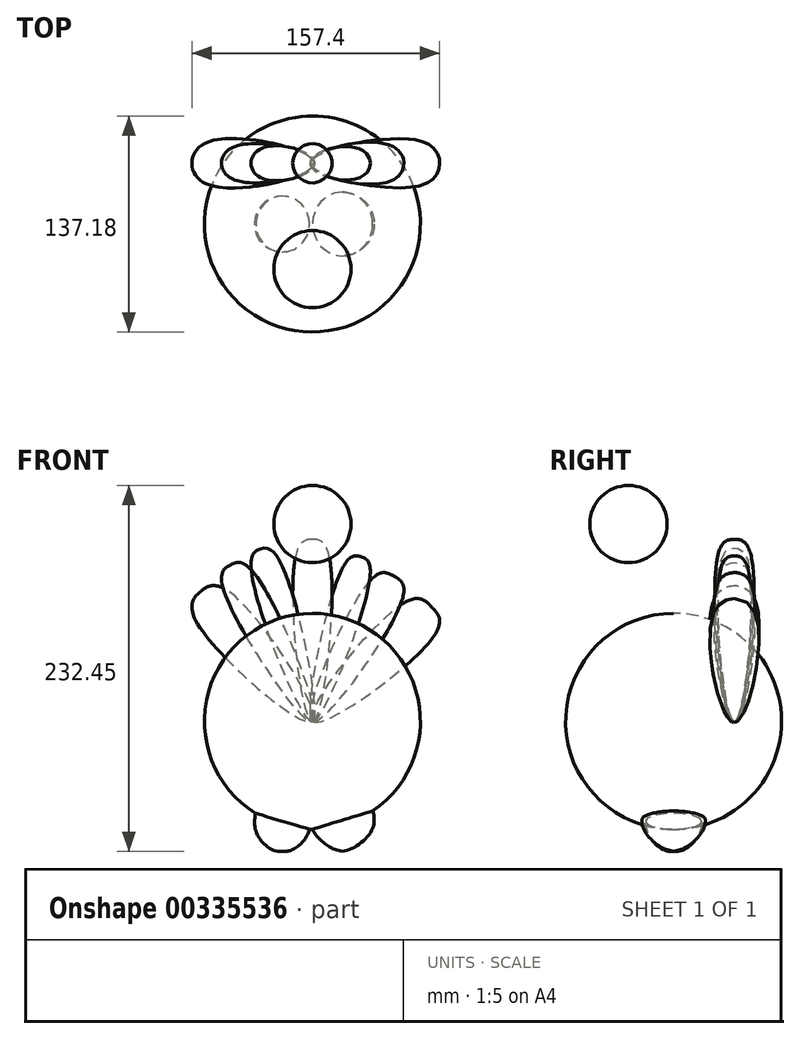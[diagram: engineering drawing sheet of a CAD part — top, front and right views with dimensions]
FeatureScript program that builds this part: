
annotation { "Feature Type Name" : "Feature", "Feature Type Description" : "" }
export const myFeature = defineFeature(function(context is Context, id is Id, definition is map)
    precondition{}
    {
        {
            var Q0;
            Q0=qCreatedBy(makeId("Front.planeOp"),FACE);
            var sketch = newSketch(context, id + "F0", { "sketchPlane" : qUnion([Q0])});
            skCircle(sketch, "E0", {"center": v(0, 0) * mm, "radius": 68.6 * mm});
            skLineSegment(sketch, "E1", {"start": v(0, 68.6) * mm, "end": v(0, -68.6) * mm});
            skSolve(sketch);
        }
        {
            var Q0;
            {var subQ0=sQuery(id+"F0.wireOp",EDGE,"E1");Q0=makeQuery(id+"F0.imprint","IMPRINT",FACE,{"disambiguationData":[TD([[makeQuery(id+"F0.imprint","IMPRINT",EDGE,{"derivedFrom":subQ0}),1.0]])]});}
            var Q1;
            Q1=sQuery(id+"F0.wireOp",EDGE,"E1");
            revolve(context, id + "F1", {"entities" : qUnion([Q0]), "axis" : qUnion([Q1]), "revolveType" : RevolveType.FULL});
        }
        {
            var Q0;
            Q0=qCreatedBy(makeId("Front.planeOp"),FACE);
            cPlane(context, id + "F2", {"entities" : qUnion([Q0]), "cplaneType" : CPlaneType.OFFSET, "offset" : 38.6 * mm, "oppositeDirection" : true, "width" : 152.4 * mm, "height" : 152.4 * mm});
        }
        {
            var Q0;
            Q0=qCreatedBy(id+"F2.planeOp",FACE);
            var sketch = newSketch(context, id + "F3", { "sketchPlane" : qUnion([Q0])});
            skLineSegment(sketch, "E2", {"start": v(0, 0) * mm, "end": v(0, 115.63) * mm});
            skFitSpline(sketch, "E3", {"points": [v(0, 0) * mm, v(9.62, 105.29) * mm, v(0, 115.63) * mm, v(-10.38, 106.07) * mm, v(0, 0) * mm]});
            skSolve(sketch);
        }
        {
            var Q0;
            {var subQ0=sQuery(id+"F3.wireOp",EDGE,"E2");Q0=makeQuery(id+"F3.imprint","IMPRINT",FACE,{"disambiguationData":[TD([[makeQuery(id+"F3.imprint","IMPRINT",EDGE,{"derivedFrom":subQ0}),1.0]])]});}
            var Q1;
            Q1=sQuery(id+"F3.wireOp",EDGE,"E2");
            revolve(context, id + "F4", {"entities" : qUnion([Q0]), "axis" : qUnion([Q1]), "revolveType" : RevolveType.FULL});
        }
        {
            var Q0;
            Q0=qCreatedBy(id+"F2.planeOp",FACE);
            var sketch = newSketch(context, id + "F5", { "sketchPlane" : qUnion([Q0])});
            skLineSegment(sketch, "E4", {"start": v(0, 0) * mm, "end": v(-32.93, 109.56) * mm});
            skFitSpline(sketch, "E5", {"points": [v(0, 0) * mm, v(-38.97, 97.8) * mm, v(-32.93, 109.56) * mm, v(-22.82, 103.73) * mm, v(0, 0) * mm]});
            skSolve(sketch);
        }
        {
            var Q0;
            Q0=qCreatedBy(id+"F2.planeOp",FACE);
            var sketch = newSketch(context, id + "F6", { "sketchPlane" : qUnion([Q0])});
            skLineSegment(sketch, "E6", {"start": v(0, 0) * mm, "end": v(30.76, 104.61) * mm});
            skFitSpline(sketch, "E7", {"points": [v(0, 0) * mm, v(36.37, 93.52) * mm, v(30.76, 104.61) * mm, v(20.18, 99.28) * mm, v(0, 0) * mm]});
            skSolve(sketch);
        }
        {
            var Q0;
            {var subQ0=sQuery(id+"F5.wireOp",EDGE,"E4");Q0=makeQuery(id+"F5.imprint","IMPRINT",FACE,{"disambiguationData":[TD([[makeQuery(id+"F5.imprint","IMPRINT",EDGE,{"derivedFrom":subQ0}),1.0]])]});}
            var Q1;
            Q1=sQuery(id+"F5.wireOp",EDGE,"E4");
            revolve(context, id + "F7", {"entities" : qUnion([Q0]), "axis" : qUnion([Q1]), "revolveType" : RevolveType.FULL});
        }
        {
            var Q0;
            {var subQ0=sQuery(id+"F6.wireOp",EDGE,"E6");Q0=makeQuery(id+"F6.imprint","IMPRINT",FACE,{"disambiguationData":[TD([[makeQuery(id+"F6.imprint","IMPRINT",EDGE,{"derivedFrom":subQ0}),1.0]])]});}
            var Q1;
            Q1=sQuery(id+"F6.wireOp",EDGE,"E6");
            revolve(context, id + "F8", {"entities" : qUnion([Q0]), "axis" : qUnion([Q1]), "revolveType" : RevolveType.FULL});
        }
        {
            var Q0;
            Q0=qCreatedBy(id+"F2.planeOp",FACE);
            var sketch = newSketch(context, id + "F9", { "sketchPlane" : qUnion([Q0])});
            skLineSegment(sketch, "E8", {"start": v(0, 0) * mm, "end": v(-52.13, 99.29) * mm});
            skFitSpline(sketch, "E9", {"points": [v(0, 0) * mm, v(-38.63, 96.1) * mm, v(-52.13, 99.29) * mm, v(-57.26, 86.85) * mm, v(0, 0) * mm]});
            skSolve(sketch);
        }
        {
            var Q0;
            Q0=qCreatedBy(id+"F2.planeOp",FACE);
            var sketch = newSketch(context, id + "F10", { "sketchPlane" : qUnion([Q0])});
            skLineSegment(sketch, "E10", {"start": v(0, 0) * mm, "end": v(51.8, 92.22) * mm});
            skFitSpline(sketch, "E11", {"points": [v(0, 0) * mm, v(38.08, 90.78) * mm, v(51.8, 92.22) * mm, v(57.33, 80.06) * mm, v(0, 0) * mm]});
            skSolve(sketch);
        }
        {
            var Q0;
            Q0=qCreatedBy(id+"F2.planeOp",FACE);
            var sketch = newSketch(context, id + "F11", { "sketchPlane" : qUnion([Q0])});
            skLineSegment(sketch, "E12", {"start": v(0, 0) * mm, "end": v(75.7, 72.5) * mm});
            skFitSpline(sketch, "E13", {"points": [v(0, 0) * mm, v(60.06, 76.24) * mm, v(75.7, 72.5) * mm, v(75.7, 56.25) * mm, v(0, 0) * mm]});
            skSolve(sketch);
        }
        {
            var Q0;
            Q0=qCreatedBy(id+"F2.planeOp",FACE);
            var sketch = newSketch(context, id + "F12", { "sketchPlane" : qUnion([Q0])});
            skLineSegment(sketch, "E14", {"start": v(0, 0) * mm, "end": v(-71.26, 82.25) * mm});
            skFitSpline(sketch, "E15", {"points": [v(0, 0) * mm, v(-57.38, 81.72) * mm, v(-71.26, 82.25) * mm, v(-74.63, 65.2) * mm, v(0, 0) * mm]});
            skSolve(sketch);
        }
        {
            var Q0;
            {var subQ0=sQuery(id+"F10.wireOp",EDGE,"E10");Q0=makeQuery(id+"F10.imprint","IMPRINT",FACE,{"disambiguationData":[TD([[makeQuery(id+"F10.imprint","IMPRINT",EDGE,{"derivedFrom":subQ0}),1.0]])]});}
            var Q1;
            Q1=sQuery(id+"F10.wireOp",EDGE,"E10");
            revolve(context, id + "F13", {"entities" : qUnion([Q0]), "axis" : qUnion([Q1]), "revolveType" : RevolveType.FULL});
        }
        {
            var Q0;
            {var subQ0=sQuery(id+"F11.wireOp",EDGE,"E12");Q0=makeQuery(id+"F11.imprint","IMPRINT",FACE,{"disambiguationData":[TD([[makeQuery(id+"F11.imprint","IMPRINT",EDGE,{"derivedFrom":subQ0}),1.0]])]});}
            var Q1;
            Q1=sQuery(id+"F11.wireOp",EDGE,"E12");
            revolve(context, id + "F14", {"entities" : qUnion([Q0]), "axis" : qUnion([Q1]), "revolveType" : RevolveType.FULL});
        }
        {
            var Q0;
            {var subQ0=sQuery(id+"F9.wireOp",EDGE,"E8");Q0=makeQuery(id+"F9.imprint","IMPRINT",FACE,{"disambiguationData":[TD([[makeQuery(id+"F9.imprint","IMPRINT",EDGE,{"derivedFrom":subQ0}),1.0]])]});}
            var Q1;
            Q1=sQuery(id+"F9.wireOp",EDGE,"E8");
            revolve(context, id + "F15", {"entities" : qUnion([Q0]), "axis" : qUnion([Q1]), "revolveType" : RevolveType.FULL});
        }
        {
            var Q0;
            {var subQ0=sQuery(id+"F12.wireOp",EDGE,"E14");Q0=makeQuery(id+"F12.imprint","IMPRINT",FACE,{"disambiguationData":[TD([[makeQuery(id+"F12.imprint","IMPRINT",EDGE,{"derivedFrom":subQ0}),1.0]])]});}
            var Q1;
            Q1=sQuery(id+"F12.wireOp",EDGE,"E14");
            revolve(context, id + "F16", {"entities" : qUnion([Q0]), "axis" : qUnion([Q1]), "revolveType" : RevolveType.FULL});
        }
        {
            var Q0;
            Q0=qCreatedBy(makeId("Top.planeOp"),FACE);
            cPlane(context, id + "F17", {"entities" : qUnion([Q0]), "cplaneType" : CPlaneType.OFFSET, "offset" : 47.24 * mm, "width" : 152.4 * mm, "height" : 152.4 * mm});
        }
        {
            var Q0;
            Q0=qCreatedBy(id+"F17.planeOp",FACE);
            var sketch = newSketch(context, id + "F18", { "sketchPlane" : qUnion([Q0])});
            skCircle(sketch, "E16", {"center": v(0, -28.77) * mm, "radius": 12.7 * mm});
            skSolve(sketch);
        }
        {
            var Q0;
            Q0=qCreatedBy(makeId("Front.planeOp"),FACE);
            cPlane(context, id + "F19", {"entities" : qUnion([Q0]), "cplaneType" : CPlaneType.OFFSET, "offset" : 28.65 * mm, "width" : 152.4 * mm, "height" : 152.4 * mm});
        }
        {
            var Q0;
            Q0=sQuery(id+"F18.wireOp",EDGE,"E16");
            extrude(context, id + "F20", {"bodyType" : ToolBodyType.SURFACE, "surfaceEntities" : qUnion([Q0]), "depth" : 57.15 * mm});
        }
        {
            var Q0;
            Q0=qCreatedBy(id+"F19.planeOp",FACE);
            var sketch = newSketch(context, id + "F21", { "sketchPlane" : qUnion([Q0])});
            skCircle(sketch, "E17", {"center": v(0, 125.28) * mm, "radius": 24.52 * mm});
            skLineSegment(sketch, "E18", {"start": v(0, 149.8) * mm, "end": v(0, 100.77) * mm});
            skSolve(sketch);
        }
        {
            var Q0;
            {var subQ0=sQuery(id+"F21.wireOp",EDGE,"E18");Q0=makeQuery(id+"F21.imprint","IMPRINT",FACE,{"disambiguationData":[TD([[makeQuery(id+"F21.imprint","IMPRINT",EDGE,{"derivedFrom":subQ0}),1.0]])]});}
            var Q1;
            Q1=sQuery(id+"F21.wireOp",EDGE,"E18");
            revolve(context, id + "F22", {"entities" : qUnion([Q0]), "axis" : qUnion([Q1]), "revolveType" : RevolveType.FULL});
        }
        {
            var Q0;
            Q0=qCreatedBy(makeId("Front.planeOp"),FACE);
            var sketch = newSketch(context, id + "F23", { "sketchPlane" : qUnion([Q0])});
            skLineSegment(sketch, "E19", {"start": v(0, 0) * mm, "end": v(0, -38.1) * mm});
            skLineSegment(sketch, "E20", {"start": v(0, -38.1) * mm, "end": v(-19.05, -38.1) * mm});
            skLineSegment(sketch, "E21", {"start": v(0, -38.1) * mm, "end": v(19.05, -38.1) * mm});
            skLineSegment(sketch, "E22", {"start": v(19.05, -38.1) * mm, "end": v(19.05, -82.55) * mm});
            skFitSpline(sketch, "E23", {"points": [v(19.05, -38.1) * mm, v(35.55, -51.4) * mm, v(37.85, -68.82) * mm, v(19.05, -82.55) * mm, v(6.74, -75.22) * mm, v(5.9, -53.17) * mm, v(19.05, -38.1) * mm]});
            skSolve(sketch);
        }
        {
            var Q0;
            {var subQ0=sQuery(id+"F23.wireOp",EDGE,"E22");Q0=makeQuery(id+"F23.imprint","IMPRINT",FACE,{"disambiguationData":[TD([[makeQuery(id+"F23.imprint","IMPRINT",EDGE,{"derivedFrom":subQ0}),1.0]])]});}
            var Q1;
            Q1=sQuery(id+"F23.wireOp",EDGE,"E22");
            revolve(context, id + "F24", {"operationType" : NewBodyOperationType.ADD, "entities" : qUnion([Q0]), "axis" : qUnion([Q1]), "revolveType" : RevolveType.FULL});
        }
        {
            var Q0;
            Q0=qCreatedBy(makeId("Front.planeOp"),FACE);
            var sketch = newSketch(context, id + "F25", { "sketchPlane" : qUnion([Q0])});
            skLineSegment(sketch, "E24", {"start": v(0, 0) * mm, "end": v(0, -25.4) * mm});
            skLineSegment(sketch, "E25", {"start": v(0, -25.4) * mm, "end": v(-19.05, -25.4) * mm});
            skLineSegment(sketch, "E26", {"start": v(-19.05, -25.4) * mm, "end": v(-19.05, -44.45) * mm});
            skLineSegment(sketch, "E27", {"start": v(-19.05, -44.45) * mm, "end": v(-19.05, -82.55) * mm});
            skFitSpline(sketch, "E28", {"points": [v(-19.05, -44.45) * mm, v(-5.94, -50.9) * mm, v(-2.53, -70.62) * mm, v(-19.05, -82.55) * mm, v(-33.1, -65.57) * mm, v(-31.44, -49.94) * mm, v(-19.05, -44.45) * mm]});
            skSolve(sketch);
        }
        {
            var Q0;
            {var subQ0=sQuery(id+"F25.wireOp",EDGE,"E27");Q0=makeQuery(id+"F25.imprint","IMPRINT",FACE,{"disambiguationData":[TD([[makeQuery(id+"F25.imprint","IMPRINT",EDGE,{"derivedFrom":subQ0}),1.0]])]});}
            var Q1;
            Q1=sQuery(id+"F25.wireOp",EDGE,"E27");
            revolve(context, id + "F26", {"operationType" : NewBodyOperationType.ADD, "entities" : qUnion([Q0]), "axis" : qUnion([Q1]), "revolveType" : RevolveType.FULL});
        }
        {
            var Q0;
            Q0=qCreatedBy(makeId("Top.planeOp"),FACE);
            cPlane(context, id + "F27", {"entities" : qUnion([Q0]), "cplaneType" : CPlaneType.OFFSET, "offset" : 77.47 * mm, "oppositeDirection" : true, "width" : 152.4 * mm, "height" : 152.4 * mm});
        }
    });
